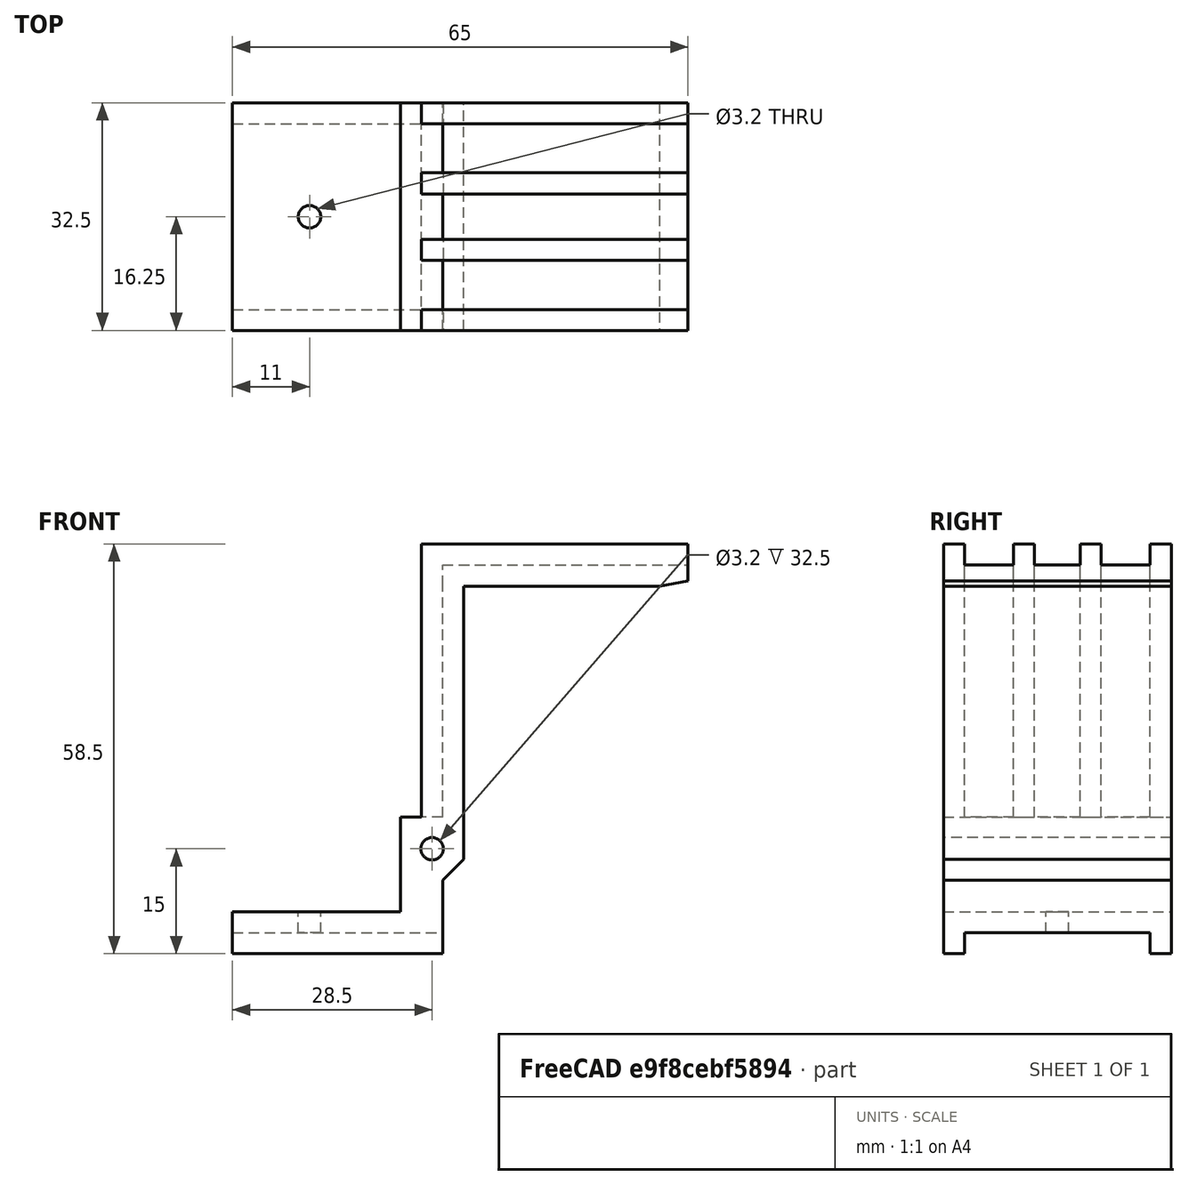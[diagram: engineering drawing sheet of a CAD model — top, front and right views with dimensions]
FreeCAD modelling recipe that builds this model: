
FCSTD DOCUMENT  (FreeCAD 0.16R6707 (Git))
Label: xmaxx-back-clasp
License: All rights reserved
LicenseURL: http://en.wikipedia.org/wiki/All_rights_reserved
objects: Part::Box×18, Part::Cut×5, Part::Cylinder×2, Part::MultiFuse×1
note: 26 computed .brp shape members not serialized (recipe doc carries the construction recipe); baked Part::Feature solids carry a one-line shape summary decoded from their .brp

FEATURE [Part::Box] Box  label="Cube"
  Height = 42.5
  Length = 3
  Width = 32.5
FEATURE [Part::Box] Box001  label="Cube001"
  Height = 3
  Length = 35
  Placement = pos=(0,0,42.5) rot=(0,0,1;0rad)
  Width = 32.5
FEATURE [Part::Box] Box002  label="Cube002"
  Height = 3
  Length = 35
  Placement = pos=(0,0,45.5) rot=(0,0,1;0rad)
  Width = 3
FEATURE [Part::Box] Box003  label="Cube003"
  Height = 3
  Length = 35
  Placement = pos=(0,29.5,45.5) rot=(0,0,1;0rad)
  Width = 3
FEATURE [Part::Box] Box004  label="Cube004"
  Height = 3
  Length = 35
  Placement = pos=(0,10,45.5) rot=(0,0,1;0rad)
  Width = 3
FEATURE [Part::Box] Box005  label="Cube005"
  Height = 3
  Length = 35
  Placement = pos=(0,19.5,45.5) rot=(0,0,1;0rad)
  Width = 3
FEATURE [Part::Box] Box006  label="Cube006"
  Height = 10
  Length = 10
  Placement = pos=(29,0,32) rot=(0,-1,0;0.174533rad)
  Width = 32.5
FEATURE [Part::Box] Box007  label="Cube007"
  Height = 13.5
  Length = 9
  Placement = pos=(-6,0,-4) rot=(0,0,1;0rad)
  Width = 32.5
FEATURE [Part::Box] Box008  label="Cube008"
  Height = 52
  Length = 3
  Placement = pos=(-3,0,-3.5) rot=(0,0,1;0rad)
  Width = 3
FEATURE [Part::Box] Box009  label="Cube009"
  Height = 52
  Length = 3
  Placement = pos=(-3,29.5,-3.5) rot=(0,0,1;0rad)
  Width = 3
FEATURE [Part::Box] Box010  label="Cube010"
  Height = 52
  Length = 3
  Placement = pos=(-3,19.5,-3.5) rot=(0,0,1;0rad)
  Width = 3
FEATURE [Part::Box] Box011  label="Cube011"
  Height = 52
  Length = 3
  Placement = pos=(-3,10,-3.5) rot=(0,0,1;0rad)
  Width = 3
FEATURE [Part::Box] Box012  label="Cube012"
  Height = 6.5
  Length = 3
  Placement = pos=(0,0,-6.5) rot=(0,0,1;0rad)
  Width = 32.5
FEATURE [Part::Box] Box013  label="Cube013"
  Height = 3
  Length = 30
  Placement = pos=(-30,0,-7) rot=(0,0,1;0rad)
  Width = 32.5
FEATURE [Part::Box] Box014  label="Cube014"
  Height = 3
  Length = 30
  Placement = pos=(-30,0,-10) rot=(0,0,1;0rad)
  Width = 3
FEATURE [Part::Box] Box015  label="Cube015"
  Height = 3
  Length = 30
  Placement = pos=(-30,29.5,-10) rot=(0,0,1;0rad)
  Width = 3
FEATURE [Part::Cylinder] Cylinder
  Angle = 360
  Height = 10
  Placement = pos=(-19,16.25,-8) rot=(0,0,1;0rad)
  Radius = 1.6
FEATURE [Part::Cylinder] Cylinder001
  Angle = 360
  Height = 35
  Placement = pos=(-1.5,33,5) rot=(1,0,0;1.5708rad)
  Radius = 1.6
FEATURE [Part::MultiFuse] Fusion
  Shapes = -> [Box,Box001,Box002,Box003,Box004,Box005,Box007,Box008,Box009,Box010,Box011,Box012,Box013,Box014,Box015]
FEATURE [Part::Cut] Cut
  Base = -> Fusion
  Tool = -> Box006
FEATURE [Part::Cut] Cut001
  Base = -> Cut
  Tool = -> Cylinder
FEATURE [Part::Cut] Cut002
  Base = -> Cut001
  Tool = -> Cylinder001
FEATURE [Part::Box] Box016  label="Cube016"
  Height = 15
  Length = 3
  Placement = pos=(0,0,-14.5) rot=(0,0,1;0rad)
  Width = 32.5
FEATURE [Part::Cut] Cut003
  Base = -> Cut002
  Tool = -> Box016
FEATURE [Part::Box] Box017  label="Cube017"
  Height = 5
  Length = 5
  Placement = pos=(0,0,0.5) rot=(0,1,0;0.785398rad)
  Width = 32.5
FEATURE [Part::Cut] Cut004
  Base = -> Cut003
  Tool = -> Box017
